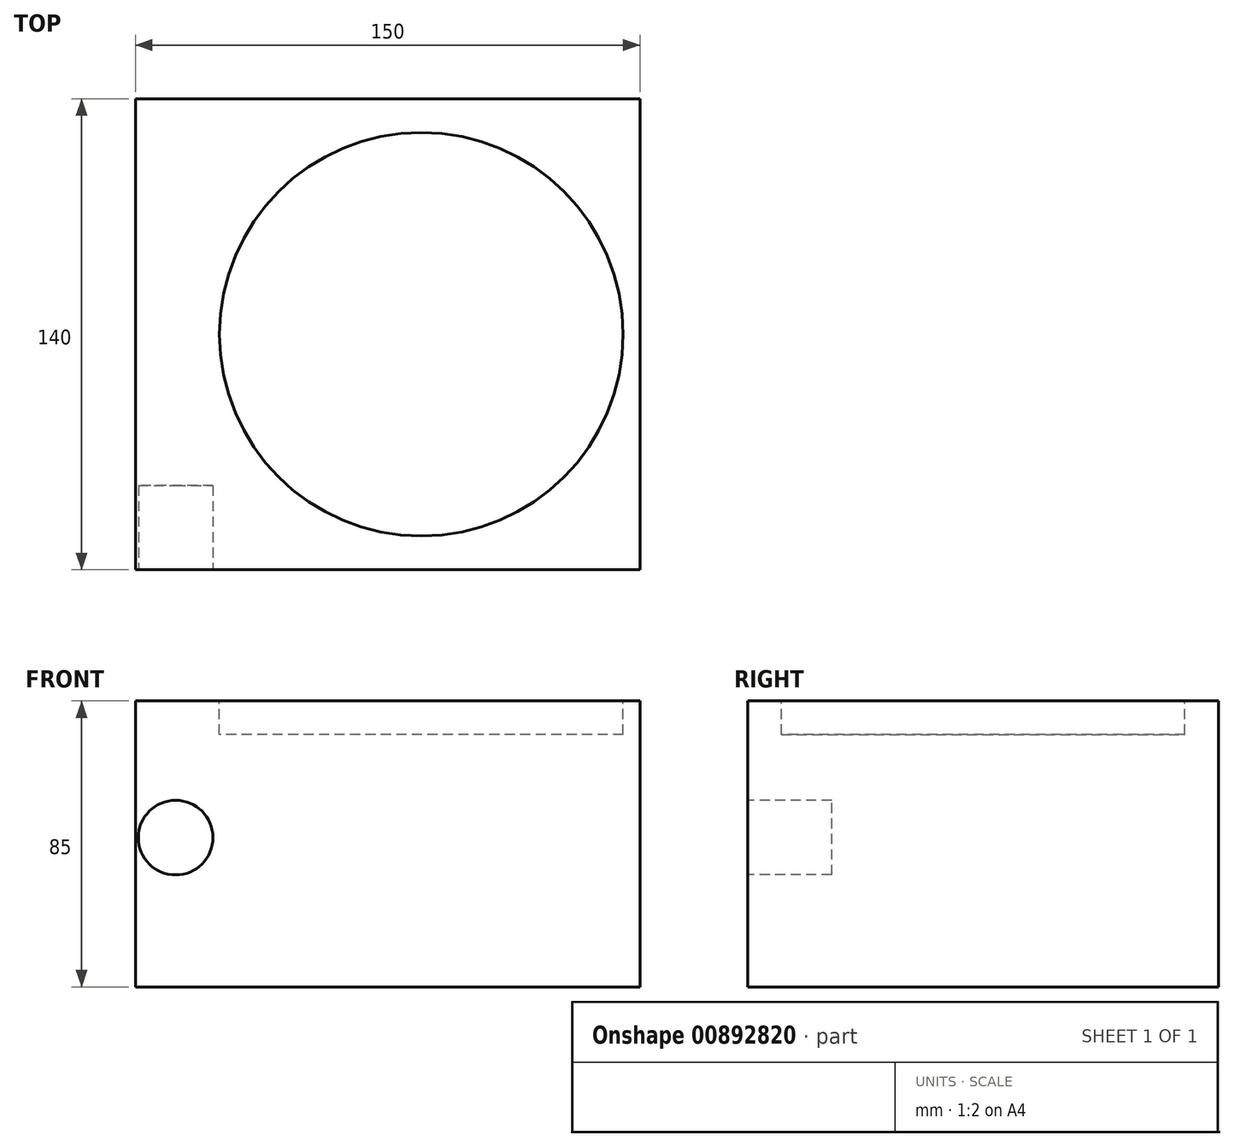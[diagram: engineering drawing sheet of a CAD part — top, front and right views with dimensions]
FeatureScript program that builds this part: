
annotation { "Feature Type Name" : "Feature", "Feature Type Description" : "" }
export const myFeature = defineFeature(function(context is Context, id is Id, definition is map)
    precondition{}
    {
        {
            var Q0;
            Q0=qCreatedBy(makeId("Top.planeOp"),FACE);
            var sketch = newSketch(context, id + "F0", { "sketchPlane" : qUnion([Q0])});
            skLineSegment(sketch, "E0.bottom", {"start": v(-75, -70) * mm, "end": v(75, -70) * mm});
            skLineSegment(sketch, "E0.top", {"start": v(-75, 70) * mm, "end": v(75, 70) * mm});
            skLineSegment(sketch, "E0.left", {"start": v(-75, -70) * mm, "end": v(-75, 70) * mm});
            skLineSegment(sketch, "E0.right", {"start": v(75, -70) * mm, "end": v(75, 70) * mm});
            skPoint(sketch, "E0.middle", {"position": v(0, 0) * mm});
            skSolve(sketch);
        }
        {
            var Q0;
            Q0=makeQuery(id+"F0.imprint","IMPRINT",FACE,{"disambiguationData":[TD([[makeQuery(id+"F0.imprint","IMPRINT",EDGE,{"derivedFrom":sQuery(id+"F0.wireOp",EDGE,"E0.bottom")}),1.0]])]});
            extrude(context, id + "F1", {"entities" : qUnion([Q0]), "depth" : 85 * mm, "offsetDistance" : 25 * mm});
        }
        {
            var Q0;
            Q0=makeQuery(id+"F1.opExtrude","SWEPT_FACE",FACE,{"disambiguationData":[OSD([sQuery(id+"F0.wireOp",EDGE,"E0.bottom")])]});
            var sketch = newSketch(context, id + "F2", { "sketchPlane" : qUnion([Q0])});
            skCircle(sketch, "E1", {"center": v(-63.03, 44.38) * mm, "radius": 11.09 * mm});
            skSolve(sketch);
        }
        {
            var Q0;
            Q0 = qSketchRegion(id + "F2", true);
            extrude(context, id + "F3", {"entities" : qUnion([Q0]), "operationType" : NewBodyOperationType.REMOVE, "oppositeDirection" : true, "depth" : 25 * mm, "offsetDistance" : 25 * mm});
        }
        {
            var Q0;
            Q0=makeQuery(id+"F1.opExtrude","CAP_FACE",FACE,{"disambiguationData":[OSD([sQuery(id+"F0.wireOp",EDGE,"E0.bottom"),sQuery(id+"F0.wireOp",EDGE,"E0.top"),sQuery(id+"F0.wireOp",EDGE,"E0.left"),sQuery(id+"F0.wireOp",EDGE,"E0.right")])],"isStart":false});
            var sketch = newSketch(context, id + "F4", { "sketchPlane" : qUnion([Q0])});
            skCircle(sketch, "E2", {"center": v(10, 0) * mm, "radius": 60 * mm});
            skSolve(sketch);
        }
        {
            var Q0;
            Q0=makeQuery(id+"F4.imprint","IMPRINT",FACE,{"disambiguationData":[TD([[makeQuery(id+"F4.imprint","IMPRINT",EDGE,{"derivedFrom":sQuery(id+"F4.wireOp",EDGE,"E2")}),1.0]])]});
            extrude(context, id + "F5", {"entities" : qUnion([Q0]), "operationType" : NewBodyOperationType.REMOVE, "oppositeDirection" : true, "depth" : 10 * mm, "offsetDistance" : 25 * mm});
        }
    });
